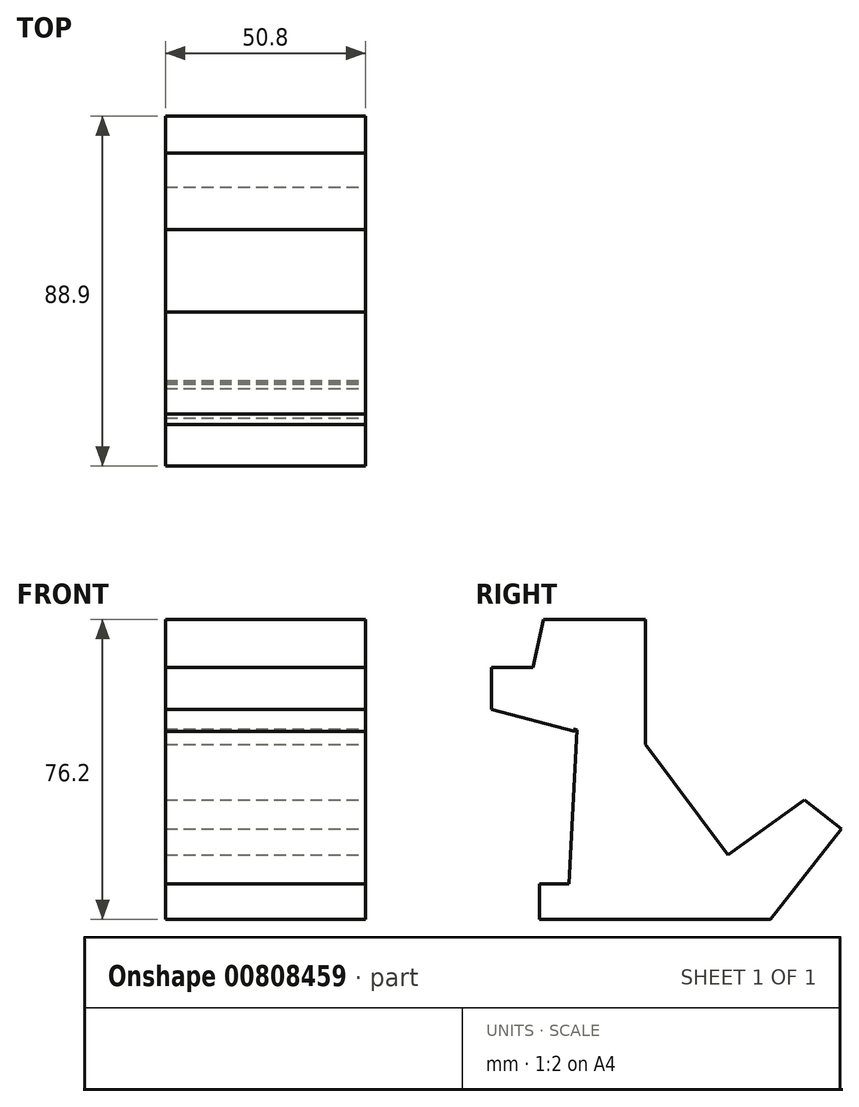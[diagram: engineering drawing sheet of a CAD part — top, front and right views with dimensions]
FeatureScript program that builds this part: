
annotation { "Feature Type Name" : "Feature", "Feature Type Description" : "" }
export const myFeature = defineFeature(function(context is Context, id is Id, definition is map)
    precondition{}
    {
        {
            var Q0;
            Q0=qCreatedBy(makeId("Right.planeOp"),FACE);
            var sketch = newSketch(context, id + "F0", { "sketchPlane" : qUnion([Q0])});
            skLineSegment(sketch, "E0", {"start": v(0, 0) * mm, "end": v(88.9, 0) * mm});
            skLineSegment(sketch, "E1", {"start": v(88.9, 0) * mm, "end": v(88.9, 76.2) * mm});
            skLineSegment(sketch, "E2", {"start": v(88.9, 76.2) * mm, "end": v(0, 76.2) * mm});
            skLineSegment(sketch, "E3", {"start": v(0, 76.2) * mm, "end": v(0, 0) * mm});
            skSolve(sketch);
        }
        {
            var Q0;
            Q0=makeQuery(id+"F0.imprint","IMPRINT",FACE,{"disambiguationData":[TD([[makeQuery(id+"F0.imprint","IMPRINT",EDGE,{"derivedFrom":sQuery(id+"F0.wireOp",EDGE,"E0")}),1.0]])]});
            extrude(context, id + "F1", {"entities" : qUnion([Q0]), "depth" : 50.8 * mm, "offsetDistance" : 25.4 * mm});
        }
        {
            var Q0;
            Q0=makeQuery(id+"F1.opExtrude","CAP_FACE",FACE,{"disambiguationData":[OSD([sQuery(id+"F0.wireOp",EDGE,"E0"),sQuery(id+"F0.wireOp",EDGE,"E1"),sQuery(id+"F0.wireOp",EDGE,"E2"),sQuery(id+"F0.wireOp",EDGE,"E3")])],"isStart":false});
            var sketch = newSketch(context, id + "F2", { "sketchPlane" : qUnion([Q0])});
            skLineSegment(sketch, "E4", {"start": v(0, 64.02) * mm, "end": v(10.6, 64.02) * mm});
            skLineSegment(sketch, "E5", {"start": v(10.6, 64.02) * mm, "end": v(13.24, 76.2) * mm});
            skLineSegment(sketch, "E6", {"start": v(0, 64.02) * mm, "end": v(0, 53.18) * mm});
            skLineSegment(sketch, "E7", {"start": v(0, 53.18) * mm, "end": v(20.7, 48.69) * mm});
            skLineSegment(sketch, "E8", {"start": v(20.7, 48.69) * mm, "end": v(20.7, 0) * mm});
            skLineSegment(sketch, "E9", {"start": v(20.7, 0) * mm, "end": v(70.87, 0) * mm});
            skLineSegment(sketch, "E10", {"start": v(70.87, 0) * mm, "end": v(88.9, 23.04) * mm});
            skLineSegment(sketch, "E11", {"start": v(88.9, 23.04) * mm, "end": v(79.5, 30.4) * mm});
            skLineSegment(sketch, "E12", {"start": v(13.24, 76.2) * mm, "end": v(39.14, 76.2) * mm});
            skLineSegment(sketch, "E13", {"start": v(39.14, 76.2) * mm, "end": v(39.14, 44.45) * mm});
            skLineSegment(sketch, "E14", {"start": v(39.14, 44.45) * mm, "end": v(60.03, 16.43) * mm});
            skLineSegment(sketch, "E15", {"start": v(60.03, 16.43) * mm, "end": v(79.5, 30.4) * mm});
            skLineSegment(sketch, "E16", {"start": v(23.28, 76.2) * mm, "end": v(26.2, 59.79) * mm});
            skPoint(sketch, "E16.endSnap0", {"position": v(26.2, 76.2) * mm});
            skLineSegment(sketch, "E17", {"start": v(26.2, 59.79) * mm, "end": v(29.76, 59.01) * mm});
            skLineSegment(sketch, "E18", {"start": v(29.76, 59.01) * mm, "end": v(33.49, 76.2) * mm});
            skSolve(sketch);
        }
        {
            var Q0;
            Q0=makeQuery(id+"F2.imprint","IMPRINT",FACE,{"disambiguationData":[TD([[makeQuery(id+"F2.imprint","IMPRINT",EDGE,{"derivedFrom":sQuery(id+"F2.wireOp",EDGE,"E4")}),-1.0]])]});
            var sketch = newSketch(context, id + "F3", { "sketchPlane" : qUnion([Q0])});
            skLineSegment(sketch, "E19", {"start": v(41.62, 5.47) * mm, "end": v(27.6, 5.47) * mm});
            skLineSegment(sketch, "E20", {"start": v(27.6, 5.47) * mm, "end": v(27.6, 0) * mm});
            skLineSegment(sketch, "E21", {"start": v(27.6, 0) * mm, "end": v(57.73, 0) * mm});
            skArc(sketch, "E22", {"start": v(57.73, 0) * mm, "mid": v(55.64, 20.29) * mm, "end": v(41.62, 5.47) * mm});
            skSolve(sketch);
        }
        {
            var Q0;
            {var subQ0=sQuery(id+"F2.wireOp",EDGE,"E4");Q0=makeQuery(id+"F2.imprint","IMPRINT",FACE,{"disambiguationData":[TD([[makeQuery(id+"F2.imprint","IMPRINT",EDGE,{"derivedFrom":subQ0}),1.0]])]});}
            var Q1;
            {var subQ1=sQuery(id+"F2.wireOp",EDGE,"E11");Q1=makeQuery(id+"F2.imprint","IMPRINT",FACE,{"disambiguationData":[TD([[makeQuery(id+"F2.imprint","IMPRINT",EDGE,{"derivedFrom":subQ1}),-1.0]])]});}
            var Q2;
            {var subQ0=sQuery(id+"F2.wireOp",EDGE,"E10");Q2=makeQuery(id+"F2.imprint","IMPRINT",FACE,{"disambiguationData":[TD([[makeQuery(id+"F2.imprint","IMPRINT",EDGE,{"derivedFrom":subQ0}),-1.0]])]});}
            extrude(context, id + "F4", {"entities" : qUnion([Q0, Q1, Q2]), "operationType" : NewBodyOperationType.REMOVE, "oppositeDirection" : true, "depth" : 50.8 * mm, "offsetDistance" : 25.4 * mm});
        }
        {
            var Q0;
            Q0=makeQuery(id+"F1.opExtrude","CAP_FACE",FACE,{"disambiguationData":[OSD([sQuery(id+"F0.wireOp",EDGE,"E0"),sQuery(id+"F0.wireOp",EDGE,"E1"),sQuery(id+"F0.wireOp",EDGE,"E2"),sQuery(id+"F0.wireOp",EDGE,"E3")])],"isStart":false});
            var sketch = newSketch(context, id + "F5", { "sketchPlane" : qUnion([Q0])});
            skLineSegment(sketch, "E23", {"start": v(0, 53.31) * mm, "end": v(21.15, 47.8) * mm});
            skLineSegment(sketch, "E24", {"start": v(21.15, 47.8) * mm, "end": v(21.15, 10.53) * mm});
            skLineSegment(sketch, "E25", {"start": v(21.15, 10.53) * mm, "end": v(12.41, 10.53) * mm});
            skLineSegment(sketch, "E26", {"start": v(12.41, 9.15) * mm, "end": v(12.41, 0) * mm});
            skLineSegment(sketch, "E27", {"start": v(0, 53.31) * mm, "end": v(0, 64.02) * mm});
            skLineSegment(sketch, "E28", {"start": v(0, 64.02) * mm, "end": v(10.6, 64.02) * mm});
            skLineSegment(sketch, "E29", {"start": v(10.6, 64.02) * mm, "end": v(21.15, 47.8) * mm});
            skSolve(sketch);
        }
        {
            var Q0;
            {var subQ3=sQuery(id+"F5.wireOp",EDGE,"E23");Q0=makeQuery(id+"F5.imprint","IMPRINT",FACE,{"disambiguationData":[TD([[makeQuery(id+"F5.imprint","IMPRINT",EDGE,{"derivedFrom":subQ3}),-1.0]])]});}
            var sketch = newSketch(context, id + "F6", { "sketchPlane" : qUnion([Q0])});
            skLineSegment(sketch, "E30", {"start": v(0, 53.33) * mm, "end": v(0, 0) * mm});
            skLineSegment(sketch, "E31", {"start": v(0, 0) * mm, "end": v(12.18, 0) * mm});
            skLineSegment(sketch, "E32", {"start": v(12.18, 0) * mm, "end": v(12.18, 9) * mm});
            skLineSegment(sketch, "E33", {"start": v(12.18, 9) * mm, "end": v(19.71, 9) * mm});
            skLineSegment(sketch, "E34", {"start": v(19.71, 9) * mm, "end": v(21.74, 48.12) * mm});
            skLineSegment(sketch, "E35", {"start": v(21.74, 48.12) * mm, "end": v(0, 53.33) * mm});
            skSolve(sketch);
        }
        {
            var Q0;
            {var subQ0=sQuery(id+"F6.wireOp",EDGE,"E31");Q0=makeQuery(id+"F6.imprint","IMPRINT",FACE,{"disambiguationData":[TD([[makeQuery(id+"F6.imprint","IMPRINT",EDGE,{"derivedFrom":subQ0}),1.0]])]});}
            extrude(context, id + "F7", {"entities" : qUnion([Q0]), "operationType" : NewBodyOperationType.REMOVE, "oppositeDirection" : true, "depth" : 50.8 * mm, "offsetDistance" : 25.4 * mm});
        }
    });
